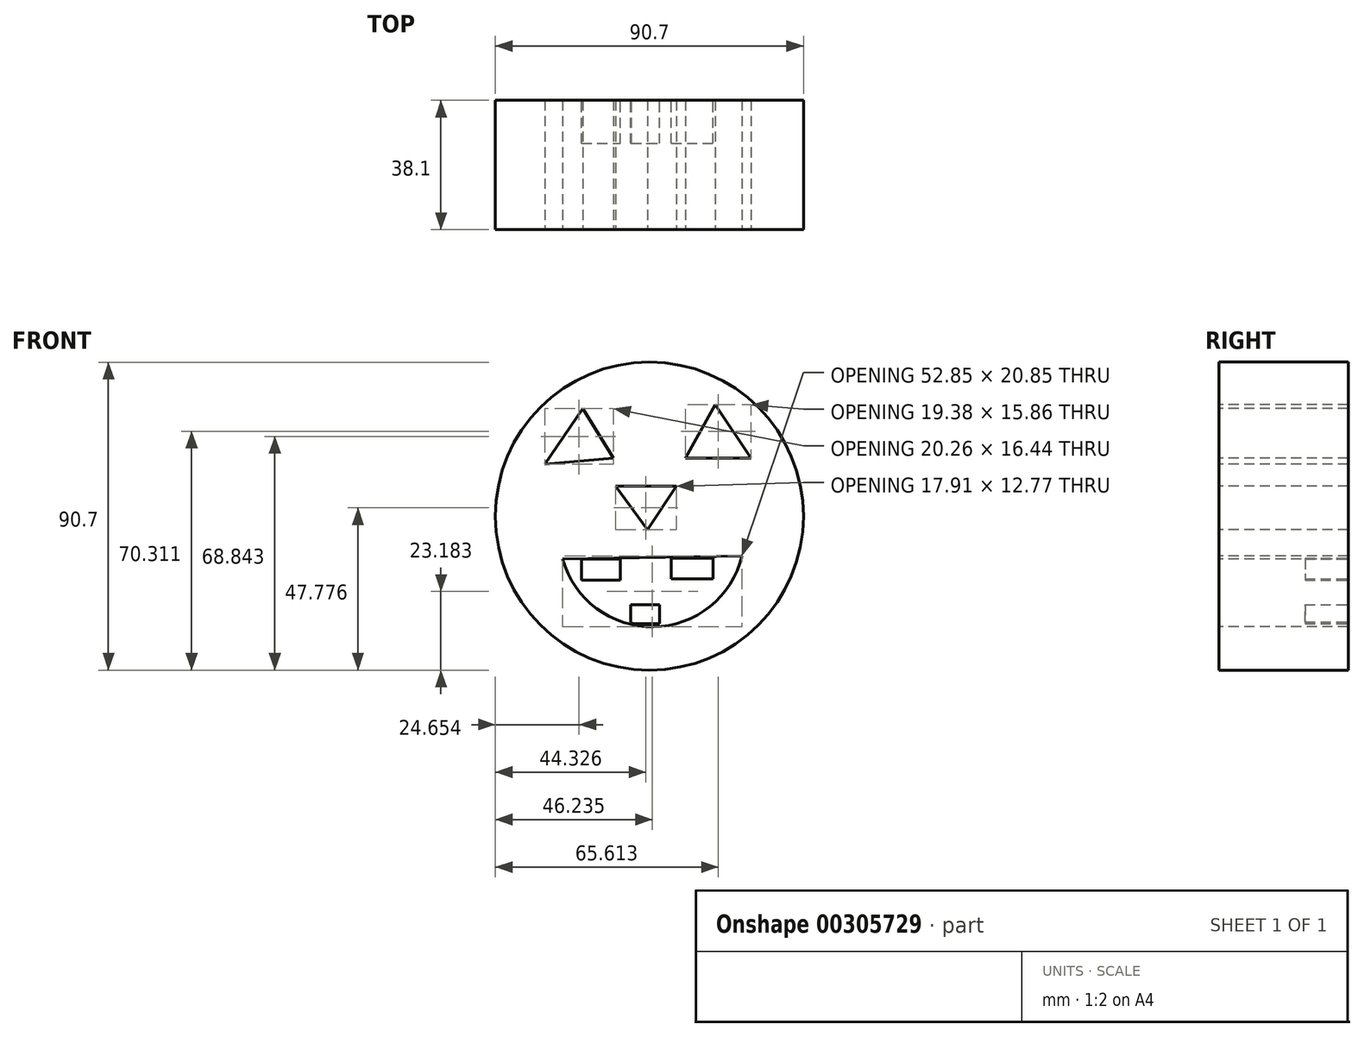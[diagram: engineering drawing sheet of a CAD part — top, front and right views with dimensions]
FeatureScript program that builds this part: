
annotation { "Feature Type Name" : "Feature", "Feature Type Description" : "" }
export const myFeature = defineFeature(function(context is Context, id is Id, definition is map)
    precondition{}
    {
        {
            var Q0;
            Q0=qCreatedBy(makeId("Front.planeOp"),FACE);
            var sketch = newSketch(context, id + "F0", { "sketchPlane" : qUnion([Q0])});
            skCircle(sketch, "E0", {"center": v(-2.94, 3.96) * mm, "radius": 45.35 * mm});
            skSolve(sketch);
        }
        {
            var Q0;
            Q0 = qSketchRegion(id + "F0", true);
            extrude(context, id + "F1", {"entities" : qUnion([Q0]), "depth" : 12.7 * mm});
        }
        {
            var Q0;
            Q0=makeQuery(id+"F1.opExtrude","CAP_FACE",FACE,{"disambiguationData":[OSD([sQuery(id+"F0.wireOp",EDGE,"E0")])],"isStart":false});
            var sketch = newSketch(context, id + "F2", { "sketchPlane" : qUnion([Q0])});
            skLineSegment(sketch, "E1", {"start": v(-33.77, 19.23) * mm, "end": v(-22.6, 35.67) * mm});
            skLineSegment(sketch, "E2", {"start": v(-22.6, 35.67) * mm, "end": v(-13.5, 21) * mm});
            skLineSegment(sketch, "E3", {"start": v(-33.77, 19.23) * mm, "end": v(-13.5, 21) * mm});
            skSolve(sketch);
        }
        {
            var Q0;
            Q0=makeQuery(id+"F2.imprint","IMPRINT",FACE,{"disambiguationData":[TD([[makeQuery(id+"F2.imprint","IMPRINT",EDGE,{"derivedFrom":sQuery(id+"F2.wireOp",EDGE,"E1")}),-1.0]])]});
            extrude(context, id + "F3", {"entities" : qUnion([Q0]), "operationType" : NewBodyOperationType.REMOVE, "oppositeDirection" : true, "depth" : 12.7 * mm});
        }
        {
            var Q0;
            Q0=makeQuery(id+"F1.opExtrude","CAP_FACE",FACE,{"disambiguationData":[OSD([sQuery(id+"F0.wireOp",EDGE,"E0")])],"isStart":false});
            var sketch = newSketch(context, id + "F4", { "sketchPlane" : qUnion([Q0])});
            skLineSegment(sketch, "E4", {"start": v(27.01, 21) * mm, "end": v(16.44, 36.85) * mm});
            skLineSegment(sketch, "E5", {"start": v(16.44, 36.85) * mm, "end": v(7.63, 21) * mm});
            skLineSegment(sketch, "E6", {"start": v(7.63, 21) * mm, "end": v(27.01, 21) * mm});
            skSolve(sketch);
        }
        {
            var Q0;
            Q0=makeQuery(id+"F4.imprint","IMPRINT",FACE,{"disambiguationData":[TD([[makeQuery(id+"F4.imprint","IMPRINT",EDGE,{"derivedFrom":sQuery(id+"F4.wireOp",EDGE,"E4")}),1.0]])]});
            extrude(context, id + "F5", {"entities" : qUnion([Q0]), "operationType" : NewBodyOperationType.REMOVE, "oppositeDirection" : true, "depth" : 12.7 * mm});
        }
        {
            var Q0;
            Q0=makeQuery(id+"F1.opExtrude","CAP_FACE",FACE,{"disambiguationData":[OSD([sQuery(id+"F0.wireOp",EDGE,"E0")])],"isStart":false});
            var sketch = newSketch(context, id + "F6", { "sketchPlane" : qUnion([Q0])});
            skArc(sketch, "E7", {"start": v(-28.48, -8.66) * mm, "mid": v(-1.72, -28.63) * mm, "end": v(24.37, -7.78) * mm});
            skLineSegment(sketch, "E8", {"start": v(-28.48, -8.66) * mm, "end": v(24.37, -7.78) * mm});
            skSolve(sketch);
        }
        {
            var Q0;
            Q0=makeQuery(id+"F6.imprint","IMPRINT",FACE,{"disambiguationData":[TD([[makeQuery(id+"F6.imprint","IMPRINT",EDGE,{"derivedFrom":sQuery(id+"F6.wireOp",EDGE,"E7")}),1.0]])]});
            extrude(context, id + "F7", {"entities" : qUnion([Q0]), "operationType" : NewBodyOperationType.REMOVE, "oppositeDirection" : true, "depth" : 12.7 * mm});
        }
        {
            var Q0;
            Q0=makeQuery(id+"F1.opExtrude","CAP_FACE",FACE,{"disambiguationData":[OSD([sQuery(id+"F0.wireOp",EDGE,"E0")])],"isStart":false});
            var sketch = newSketch(context, id + "F8", { "sketchPlane" : qUnion([Q0])});
            skLineSegment(sketch, "E9", {"start": v(-12.92, 12.77) * mm, "end": v(5, 12.77) * mm});
            skLineSegment(sketch, "E10", {"start": v(5, 12.77) * mm, "end": v(-3.52, 0) * mm});
            skLineSegment(sketch, "E11", {"start": v(-3.52, 0) * mm, "end": v(-12.92, 12.77) * mm});
            skSolve(sketch);
        }
        {
            var Q0;
            Q0=makeQuery(id+"F8.imprint","IMPRINT",FACE,{"disambiguationData":[TD([[makeQuery(id+"F8.imprint","IMPRINT",EDGE,{"derivedFrom":sQuery(id+"F8.wireOp",EDGE,"E9")}),-1.0]])]});
            extrude(context, id + "F9", {"entities" : qUnion([Q0]), "operationType" : NewBodyOperationType.REMOVE, "oppositeDirection" : true, "depth" : 25.4 * mm});
        }
        {
            var Q0;
            Q0=makeQuery(id+"F1.opExtrude","CAP_FACE",FACE,{"disambiguationData":[OSD([sQuery(id+"F0.wireOp",EDGE,"E0")])],"isStart":false});
            extrude(context, id + "F10", {"entities" : qUnion([Q0]), "operationType" : NewBodyOperationType.ADD, "depth" : 25.4 * mm});
        }
        {
            var Q0;
            Q0=qCreatedBy(makeId("Front.planeOp"),FACE);
            var sketch = newSketch(context, id + "F11", { "sketchPlane" : qUnion([Q0])});
            skLineSegment(sketch, "E12.bottom", {"start": v(-22.9, -8.66) * mm, "end": v(-11.45, -8.66) * mm});
            skLineSegment(sketch, "E12.top", {"start": v(-22.9, -14.83) * mm, "end": v(-11.45, -14.83) * mm});
            skLineSegment(sketch, "E12.left", {"start": v(-22.9, -8.66) * mm, "end": v(-22.9, -14.83) * mm});
            skLineSegment(sketch, "E12.right", {"start": v(-11.45, -8.66) * mm, "end": v(-11.45, -14.83) * mm});
            skLineSegment(sketch, "E13.bottom", {"start": v(3.52, -8.37) * mm, "end": v(15.86, -8.37) * mm});
            skLineSegment(sketch, "E13.top", {"start": v(3.52, -14.53) * mm, "end": v(15.86, -14.53) * mm});
            skLineSegment(sketch, "E13.left", {"start": v(3.52, -8.37) * mm, "end": v(3.52, -14.53) * mm});
            skLineSegment(sketch, "E13.right", {"start": v(15.86, -8.37) * mm, "end": v(15.86, -14.53) * mm});
            skLineSegment(sketch, "E14.bottom", {"start": v(-8.22, -27.16) * mm, "end": v(0, -27.16) * mm});
            skLineSegment(sketch, "E14.top", {"start": v(-8.22, -27.75) * mm, "end": v(0, -27.75) * mm});
            skLineSegment(sketch, "E14.left", {"start": v(-8.22, -27.16) * mm, "end": v(-8.22, -27.75) * mm});
            skLineSegment(sketch, "E14.right", {"start": v(0, -27.16) * mm, "end": v(0, -27.75) * mm});
            skLineSegment(sketch, "E15.bottom", {"start": v(0, -22.17) * mm, "end": v(0, -22.17) * mm});
            skLineSegment(sketch, "E15.top", {"start": v(0, -27.16) * mm, "end": v(0, -27.16) * mm});
            skLineSegment(sketch, "E15.left", {"start": v(0, -22.17) * mm, "end": v(0, -27.16) * mm});
            skLineSegment(sketch, "E15.right", {"start": v(0, -22.17) * mm, "end": v(0, -27.16) * mm});
            skLineSegment(sketch, "E16.bottom", {"start": v(-8.51, -22.17) * mm, "end": v(0, -22.17) * mm});
            skLineSegment(sketch, "E16.left", {"start": v(-8.51, -22.17) * mm, "end": v(-8.51, -22.17) * mm});
            skLineSegment(sketch, "E17.bottom", {"start": v(-8.22, -27.16) * mm, "end": v(-8.51, -27.16) * mm});
            skLineSegment(sketch, "E17.top", {"start": v(-8.22, -22.17) * mm, "end": v(-8.51, -22.17) * mm});
            skLineSegment(sketch, "E17.left", {"start": v(-8.22, -27.16) * mm, "end": v(-8.22, -22.17) * mm});
            skLineSegment(sketch, "E17.right", {"start": v(-8.51, -27.16) * mm, "end": v(-8.51, -22.17) * mm});
            skSolve(sketch);
        }
        {
            var Q0;
            Q0 = qSketchRegion(id + "F11", true);
            extrude(context, id + "F12", {"entities" : qUnion([Q0]), "depth" : 12.7 * mm});
        }
    });
